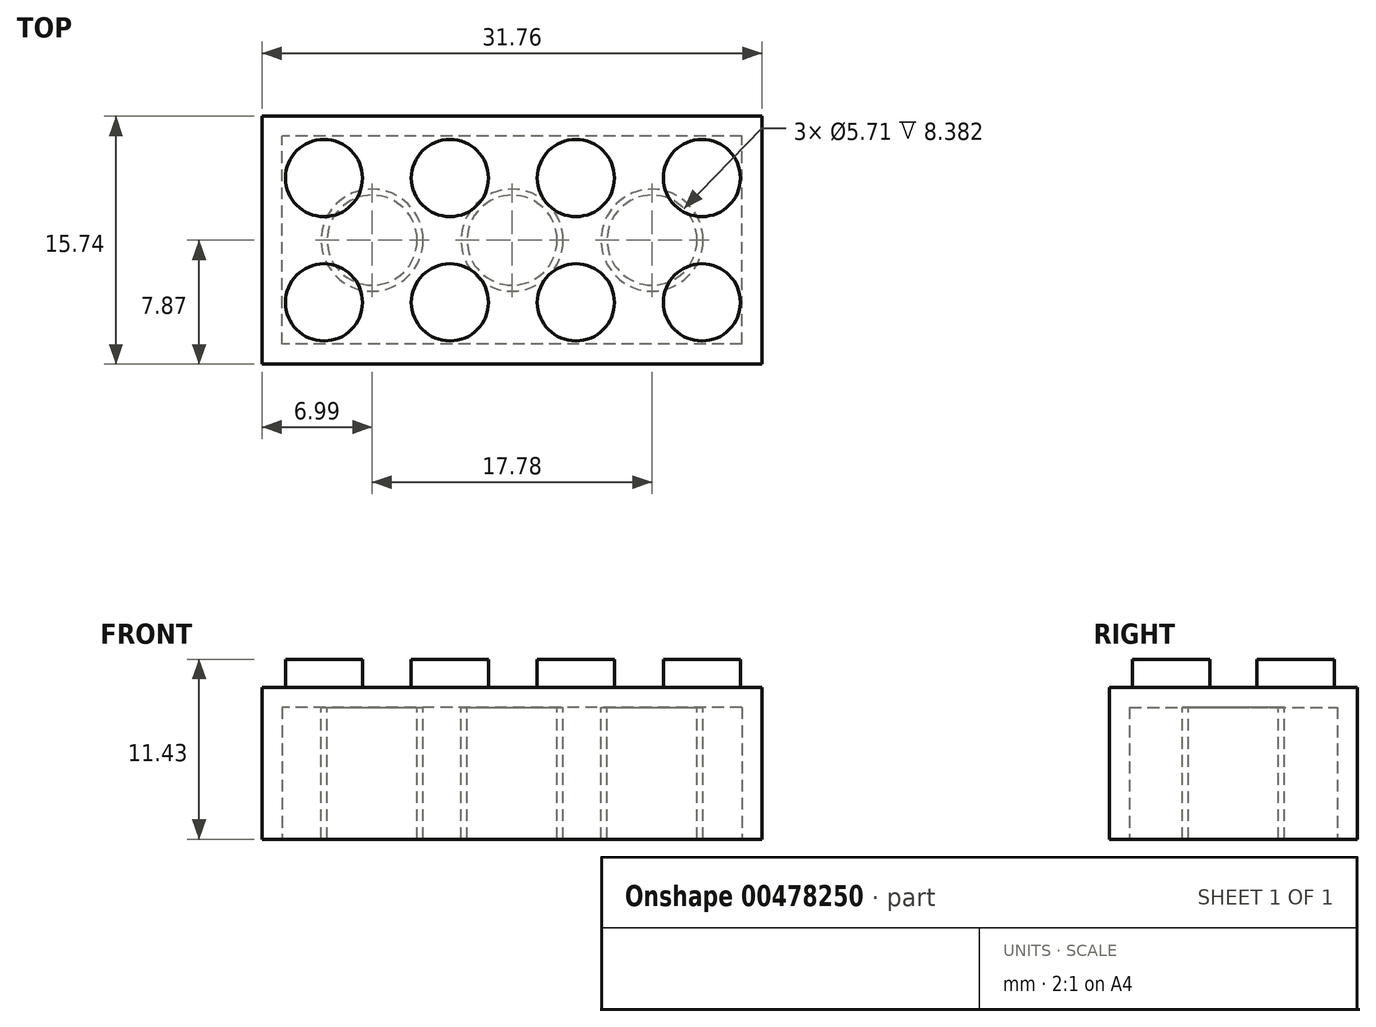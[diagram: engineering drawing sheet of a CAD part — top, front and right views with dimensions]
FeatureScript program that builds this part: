
annotation { "Feature Type Name" : "Feature", "Feature Type Description" : "" }
export const myFeature = defineFeature(function(context is Context, id is Id, definition is map)
    precondition{}
    {
        {
            var Q0;
            Q0=qCreatedBy(makeId("Top.planeOp"),FACE);
            var sketch = newSketch(context, id + "F0", { "sketchPlane" : qUnion([Q0])});
            skLineSegment(sketch, "E0.bottom", {"start": v(15.88, -7.87) * mm, "end": v(-15.88, -7.87) * mm});
            skLineSegment(sketch, "E0.top", {"start": v(15.88, 7.87) * mm, "end": v(-15.88, 7.87) * mm});
            skLineSegment(sketch, "E0.left", {"start": v(15.88, -7.87) * mm, "end": v(15.88, 7.87) * mm});
            skLineSegment(sketch, "E0.right", {"start": v(-15.88, -7.87) * mm, "end": v(-15.88, 7.87) * mm});
            skPoint(sketch, "E0.middle", {"position": v(0, 0) * mm});
            skSolve(sketch);
        }
        {
            var Q0;
            Q0 = qSketchRegion(id + "F0", true);
            extrude(context, id + "F1", {"entities" : qUnion([Q0]), "depth" : 9.65 * mm, "offsetDistance" : 25.4 * mm});
        }
        {
            var Q0;
            Q0=makeQuery(id+"F1.opExtrude","CAP_FACE",FACE,{"disambiguationData":[OSD([sQuery(id+"F0.wireOp",EDGE,"E0.bottom"),sQuery(id+"F0.wireOp",EDGE,"E0.top"),sQuery(id+"F0.wireOp",EDGE,"E0.left"),sQuery(id+"F0.wireOp",EDGE,"E0.right")])],"isStart":false});
            var sketch = newSketch(context, id + "F2", { "sketchPlane" : qUnion([Q0])});
            skCircle(sketch, "E1", {"center": v(-11.95, 3.95) * mm, "radius": 2.45 * mm});
            skCircle(sketch, "E2", {"center": v(-3.95, 3.95) * mm, "radius": 2.45 * mm});
            skCircle(sketch, "E3", {"center": v(4.05, 3.95) * mm, "radius": 2.45 * mm});
            skCircle(sketch, "E4", {"center": v(12.05, 3.95) * mm, "radius": 2.45 * mm});
            skCircle(sketch, "E5", {"center": v(-11.95, -3.95) * mm, "radius": 2.45 * mm});
            skCircle(sketch, "E6", {"center": v(-3.95, -3.95) * mm, "radius": 2.45 * mm});
            skCircle(sketch, "E7", {"center": v(4.05, -3.95) * mm, "radius": 2.45 * mm});
            skCircle(sketch, "E8", {"center": v(12.05, -3.95) * mm, "radius": 2.45 * mm});
            skSolve(sketch);
        }
        {
            var Q0;
            Q0 = qSketchRegion(id + "F2", true);
            extrude(context, id + "F3", {"entities" : qUnion([Q0]), "operationType" : NewBodyOperationType.ADD, "depth" : 1.78 * mm, "offsetDistance" : 25.4 * mm});
        }
        {
            var Q0;
            Q0=makeQuery(id+"F1.opExtrude","CAP_FACE",FACE,{"disambiguationData":[OSD([sQuery(id+"F0.wireOp",EDGE,"E0.bottom"),sQuery(id+"F0.wireOp",EDGE,"E0.top"),sQuery(id+"F0.wireOp",EDGE,"E0.left"),sQuery(id+"F0.wireOp",EDGE,"E0.right")])],"isStart":true});
            var sketch = newSketch(context, id + "F4", { "sketchPlane" : qUnion([Q0])});
            skLineSegment(sketch, "E9.bottom", {"start": v(14.6, 6.6) * mm, "end": v(-14.6, 6.6) * mm});
            skLineSegment(sketch, "E9.top", {"start": v(14.6, -6.6) * mm, "end": v(-14.6, -6.6) * mm});
            skLineSegment(sketch, "E9.left", {"start": v(14.6, 6.6) * mm, "end": v(14.6, -6.6) * mm});
            skLineSegment(sketch, "E9.right", {"start": v(-14.6, 6.6) * mm, "end": v(-14.6, -6.6) * mm});
            skPoint(sketch, "E9.middle", {"position": v(0, 0) * mm});
            skSolve(sketch);
        }
        {
            var Q0;
            Q0 = qSketchRegion(id + "F4", true);
            extrude(context, id + "F5", {"entities" : qUnion([Q0]), "operationType" : NewBodyOperationType.REMOVE, "oppositeDirection" : true, "depth" : 8.38 * mm, "offsetDistance" : 25.4 * mm});
        }
        {
            var Q0;
            Q0=makeQuery(id+"F5.boolean.opBoolean","COPY",FACE,{"derivedFrom":makeQuery(id+"F5.opExtrude","CAP_FACE",FACE,{"disambiguationData":[OSD([sQuery(id+"F4.wireOp",EDGE,"E9.bottom"),sQuery(id+"F4.wireOp",EDGE,"E9.top"),sQuery(id+"F4.wireOp",EDGE,"E9.left"),sQuery(id+"F4.wireOp",EDGE,"E9.right")])],"isStart":false})});
            var sketch = newSketch(context, id + "F6", { "sketchPlane" : qUnion([Q0])});
            skCircle(sketch, "E10", {"center": v(-8.9, 0) * mm, "radius": 3.24 * mm});
            skCircle(sketch, "E11", {"center": v(0, 0) * mm, "radius": 3.24 * mm});
            skCircle(sketch, "E12", {"center": v(8.9, 0) * mm, "radius": 3.24 * mm});
            skCircle(sketch, "E13", {"center": v(-8.9, 0) * mm, "radius": 2.86 * mm});
            skCircle(sketch, "E14", {"center": v(0, 0) * mm, "radius": 2.86 * mm});
            skCircle(sketch, "E15", {"center": v(8.9, 0) * mm, "radius": 2.86 * mm});
            skSolve(sketch);
        }
        {
            var Q0;
            Q0 = qSketchRegion(id + "F6", true);
            extrude(context, id + "F7", {"entities" : qUnion([Q0]), "operationType" : NewBodyOperationType.ADD, "depth" : 8.38 * mm, "offsetDistance" : 25.4 * mm});
        }
    });
